# Revit family: F1810
name_source: partatom
category: Plumbing Fixtures
units: mm (PartAtom-declared; Revit-internal decimal feet)

## family parameters
Classification Number = 23.45.55.21
Cut with Voids When Loaded = No
Enable Cutting in Views = No
Host = Face
Maintain Annotation Orientation = No
Part Type = Normal
Room Calculation Point = No
Round Connector Dimension = Use Radius
Shared = No

## types (5) — shared parameters
Description = PLANTING AREA DRAIN
Floor Drain Material = Paint - Sherwin Williams Paint - #952C2A - Bellwood Red
Manufacturer = MIFAB
Model = F1810
URL = WWW.MIFAB.COM
zero-valued in all types: Default Elevation, WFU

## per-type parameters (varying)
| type | Body Height | Pipe Diameter | Pipe Radius |
| 2" | 3.375 " | 2 " | 1 " |
| 3" | 3.375 " | 3 " | 1.5 " |
| 4" | 3.375 " | 4 " | 2 " |
| 5" | 3.375 " | 5 " | 2.5 " |
| 6" | 4.75 " | 6 " | 3 " |

## geometry (parser evidence)
native form markers: Blend x5, Sweep x1
no freeform markers — native parametric forms only
